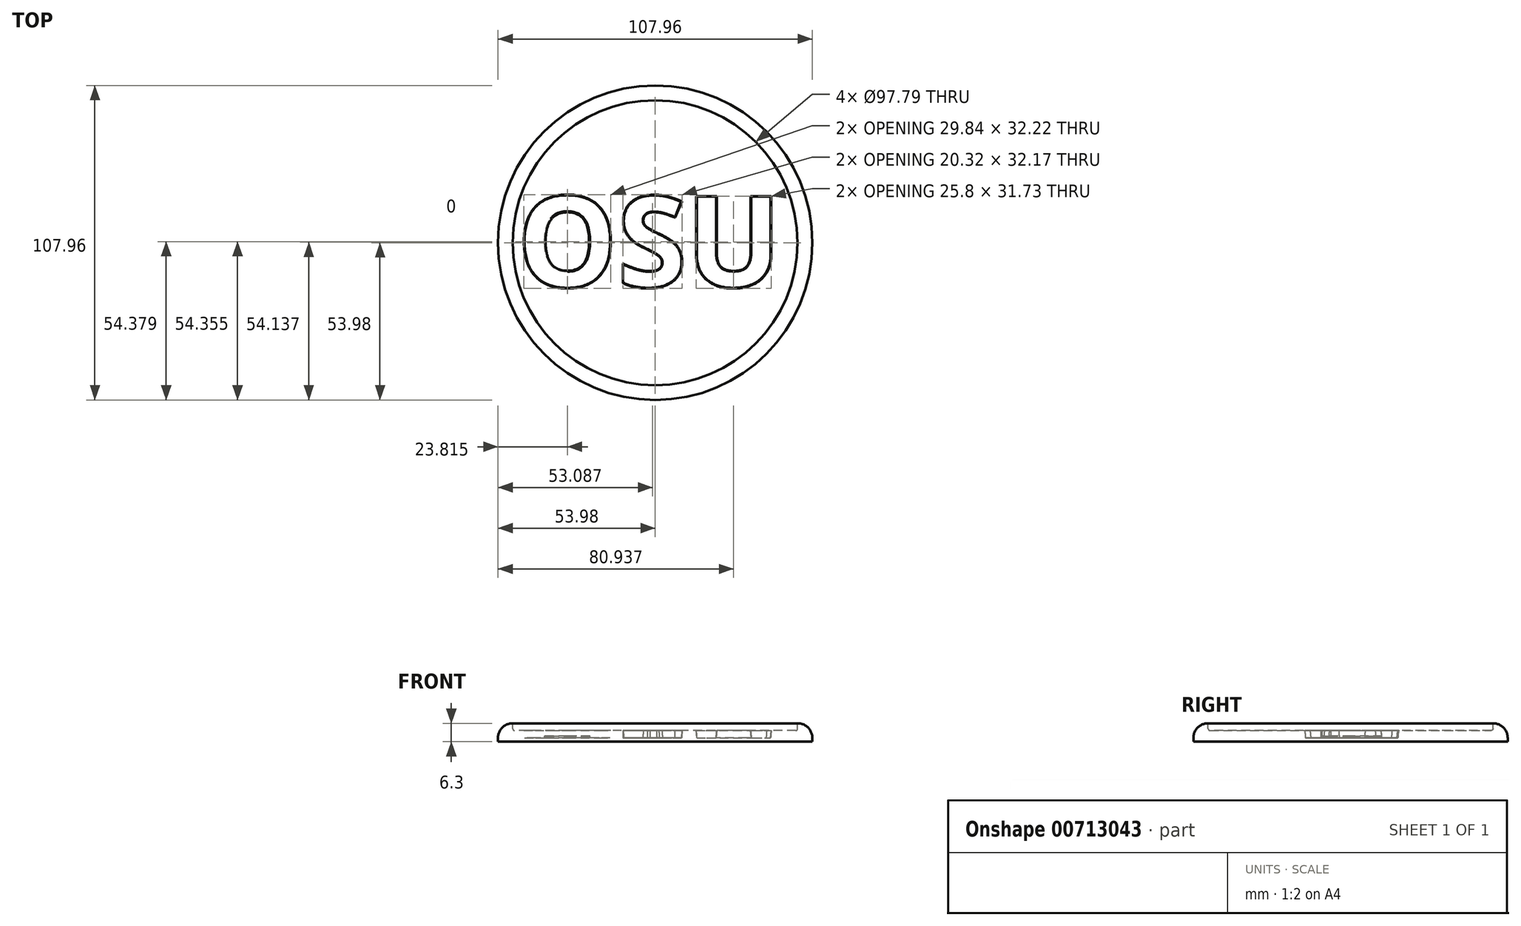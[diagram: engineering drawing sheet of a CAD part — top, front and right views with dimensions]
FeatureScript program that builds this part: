
annotation { "Feature Type Name" : "Feature", "Feature Type Description" : "" }
export const myFeature = defineFeature(function(context is Context, id is Id, definition is map)
    precondition{}
    {
        {
            var Q0;
            Q0=qCreatedBy(makeId("Top.planeOp"),FACE);
            var sketch = newSketch(context, id + "F0", { "sketchPlane" : qUnion([Q0])});
            skText(sketch, "E0", { "text": "OSU", "fontName": "OpenSans-Bold.ttf"});
            const initialGuessF0  = {"E0": [-0.0473, -0.015, 1, 0, 0.031]};
            skSetInitialGuess(sketch, initialGuessF0);
            skSolve(sketch);
        }
        {
            var Q0;
            Q0=qCreatedBy(makeId("Top.planeOp"),FACE);
            var sketch = newSketch(context, id + "F1", { "sketchPlane" : qUnion([Q0])});
            skCircle(sketch, "E1", {"center": v(0, 0) * mm, "radius": 53.98 * mm});
            skSolve(sketch);
        }
        {
            var Q0;
            Q0 = qSketchRegion(id + "F1", true);
            extrude(context, id + "F2", {"entities" : qUnion([Q0]), "oppositeDirection" : true, "depth" : 6.35 * mm, "offsetDistance" : 25.4 * mm});
        }
        {
            var Q0;
            Q0 = qSketchRegion(id + "F0", true);
            extrude(context, id + "F3", {"entities" : qUnion([Q0]), "operationType" : NewBodyOperationType.REMOVE, "oppositeDirection" : true, "depth" : 5.08 * mm, "offsetDistance" : 25.4 * mm});
        }
        {
            var Q0;
            Q0=makeQuery(id+"F2.opExtrude","CAP_EDGE",EDGE,{"disambiguationData":[OSD([sQuery(id+"F1.wireOp",EDGE,"E1")])],"isStart":true});
            fillet(context, id + "F4", {"entities" : qUnion([Q0]), "radius" : 5.08 * mm, "tangentPropagation" : true, "allowEdgeOverflow" : false});
        }
        {
            var Q0;
            Q0=makeQuery(id+"F3.boolean.opBoolean","COPY",EDGE,{"derivedFrom":makeQuery(id+"F3.opExtrude","CAP_EDGE",EDGE,{"disambiguationData":[OSD([sQuery(id+"F0.wireOp",EDGE,"E0.sketch_text.stroke-5")])],"isStart":true})});
            chamfer(context, id + "F5", {"entities" : qUnion([Q0]), "chamferType" : ChamferType.OFFSET_ANGLE, "width" : 0.5 * mm, "oppositeDirection" : false, "angle" : 85 * degree, "tangentPropagation" : true});
        }
        {
            var Q0;
            Q0=makeQuery(id+"F3.boolean.opBoolean","COPY",EDGE,{"derivedFrom":makeQuery(id+"F3.opExtrude","CAP_EDGE",EDGE,{"disambiguationData":[OSD([sQuery(id+"F0.wireOp",EDGE,"E0.sketch_text.stroke-26")])],"isStart":true})});
            var Q1;
            Q1=makeQuery(id+"F3.boolean.opBoolean","COPY",EDGE,{"derivedFrom":makeQuery(id+"F3.opExtrude","CAP_EDGE",EDGE,{"disambiguationData":[OSD([sQuery(id+"F0.wireOp",EDGE,"E0.sketch_text.stroke-23")])],"isStart":true})});
            var Q2;
            Q2=makeQuery(id+"F3.boolean.opBoolean","COPY",EDGE,{"derivedFrom":makeQuery(id+"F3.opExtrude","CAP_EDGE",EDGE,{"disambiguationData":[OSD([sQuery(id+"F0.wireOp",EDGE,"E0.sketch_text.stroke-22")])],"isStart":true})});
            var Q3;
            Q3=makeQuery(id+"F3.boolean.opBoolean","COPY",EDGE,{"derivedFrom":makeQuery(id+"F3.opExtrude","CAP_EDGE",EDGE,{"disambiguationData":[OSD([sQuery(id+"F0.wireOp",EDGE,"E0.sketch_text.stroke-14")])],"isStart":true})});
            var Q4;
            Q4=makeQuery(id+"F3.boolean.opBoolean","COPY",EDGE,{"derivedFrom":makeQuery(id+"F3.opExtrude","CAP_EDGE",EDGE,{"disambiguationData":[OSD([sQuery(id+"F0.wireOp",EDGE,"E0.sketch_text.stroke-40")])],"isStart":true})});
            var Q5;
            Q5=makeQuery(id+"F3.boolean.opBoolean","COPY",EDGE,{"derivedFrom":makeQuery(id+"F3.opExtrude","CAP_EDGE",EDGE,{"disambiguationData":[OSD([sQuery(id+"F0.wireOp",EDGE,"E0.sketch_text.stroke-37")])],"isStart":true})});
            var Q6;
            Q6=makeQuery(id+"F3.boolean.opBoolean","COPY",EDGE,{"derivedFrom":makeQuery(id+"F3.opExtrude","CAP_EDGE",EDGE,{"disambiguationData":[OSD([sQuery(id+"F0.wireOp",EDGE,"E0.sketch_text.stroke-16")])],"isStart":true})});
            var Q7;
            Q7=makeQuery(id+"F3.boolean.opBoolean","COPY",EDGE,{"derivedFrom":makeQuery(id+"F3.opExtrude","CAP_EDGE",EDGE,{"disambiguationData":[OSD([sQuery(id+"F0.wireOp",EDGE,"E0.sketch_text.stroke-15")])],"isStart":true})});
            var Q8;
            Q8=makeQuery(id+"F3.boolean.opBoolean","COPY",EDGE,{"derivedFrom":makeQuery(id+"F3.opExtrude","CAP_EDGE",EDGE,{"disambiguationData":[OSD([sQuery(id+"F0.wireOp",EDGE,"E0.sketch_text.stroke-41")])],"isStart":true})});
            var Q9;
            Q9=makeQuery(id+"F3.boolean.opBoolean","COPY",EDGE,{"derivedFrom":makeQuery(id+"F3.opExtrude","CAP_EDGE",EDGE,{"disambiguationData":[OSD([sQuery(id+"F0.wireOp",EDGE,"E0.sketch_text.stroke-39")])],"isStart":true})});
            var Q10;
            Q10=makeQuery(id+"F3.boolean.opBoolean","COPY",EDGE,{"derivedFrom":makeQuery(id+"F3.opExtrude","CAP_EDGE",EDGE,{"disambiguationData":[OSD([sQuery(id+"F0.wireOp",EDGE,"E0.sketch_text.stroke-38")])],"isStart":true})});
            var Q11;
            Q11=makeQuery(id+"F3.boolean.opBoolean","COPY",EDGE,{"derivedFrom":makeQuery(id+"F3.opExtrude","CAP_EDGE",EDGE,{"disambiguationData":[OSD([sQuery(id+"F0.wireOp",EDGE,"E0.sketch_text.stroke-36")])],"isStart":true})});
            var Q12;
            Q12=makeQuery(id+"F3.boolean.opBoolean","COPY",EDGE,{"derivedFrom":makeQuery(id+"F3.opExtrude","CAP_EDGE",EDGE,{"disambiguationData":[OSD([sQuery(id+"F0.wireOp",EDGE,"E0.sketch_text.stroke-35")])],"isStart":true})});
            var Q13;
            Q13=makeQuery(id+"F3.boolean.opBoolean","COPY",EDGE,{"derivedFrom":makeQuery(id+"F3.opExtrude","CAP_EDGE",EDGE,{"disambiguationData":[OSD([sQuery(id+"F0.wireOp",EDGE,"E0.sketch_text.stroke-34")])],"isStart":true})});
            var Q14;
            Q14=makeQuery(id+"F3.boolean.opBoolean","COPY",EDGE,{"derivedFrom":makeQuery(id+"F3.opExtrude","CAP_EDGE",EDGE,{"disambiguationData":[OSD([sQuery(id+"F0.wireOp",EDGE,"E0.sketch_text.stroke-33")])],"isStart":true})});
            var Q15;
            Q15=makeQuery(id+"F3.boolean.opBoolean","COPY",EDGE,{"derivedFrom":makeQuery(id+"F3.opExtrude","CAP_EDGE",EDGE,{"disambiguationData":[OSD([sQuery(id+"F0.wireOp",EDGE,"E0.sketch_text.stroke-32")])],"isStart":true})});
            var Q16;
            Q16=makeQuery(id+"F3.boolean.opBoolean","COPY",EDGE,{"derivedFrom":makeQuery(id+"F3.opExtrude","CAP_EDGE",EDGE,{"disambiguationData":[OSD([sQuery(id+"F0.wireOp",EDGE,"E0.sketch_text.stroke-18")])],"isStart":true})});
            var Q17;
            Q17=makeQuery(id+"F3.boolean.opBoolean","COPY",EDGE,{"derivedFrom":makeQuery(id+"F3.opExtrude","CAP_EDGE",EDGE,{"disambiguationData":[OSD([sQuery(id+"F0.wireOp",EDGE,"E0.sketch_text.stroke-19")])],"isStart":true})});
            var Q18;
            Q18=makeQuery(id+"F3.boolean.opBoolean","COPY",EDGE,{"derivedFrom":makeQuery(id+"F3.opExtrude","CAP_EDGE",EDGE,{"disambiguationData":[OSD([sQuery(id+"F0.wireOp",EDGE,"E0.sketch_text.stroke-20")])],"isStart":true})});
            var Q19;
            Q19=makeQuery(id+"F3.boolean.opBoolean","COPY",EDGE,{"derivedFrom":makeQuery(id+"F3.opExtrude","CAP_EDGE",EDGE,{"disambiguationData":[OSD([sQuery(id+"F0.wireOp",EDGE,"E0.sketch_text.stroke-21")])],"isStart":true})});
            var Q20;
            Q20=makeQuery(id+"F3.boolean.opBoolean","COPY",EDGE,{"derivedFrom":makeQuery(id+"F3.opExtrude","CAP_EDGE",EDGE,{"disambiguationData":[OSD([sQuery(id+"F0.wireOp",EDGE,"E0.sketch_text.stroke-25")])],"isStart":true})});
            var Q21;
            Q21=makeQuery(id+"F3.boolean.opBoolean","COPY",EDGE,{"derivedFrom":makeQuery(id+"F3.opExtrude","CAP_EDGE",EDGE,{"disambiguationData":[OSD([sQuery(id+"F0.wireOp",EDGE,"E0.sketch_text.stroke-24")])],"isStart":true})});
            var Q22;
            Q22=makeQuery(id+"F3.boolean.opBoolean","COPY",EDGE,{"derivedFrom":makeQuery(id+"F3.opExtrude","CAP_EDGE",EDGE,{"disambiguationData":[OSD([sQuery(id+"F0.wireOp",EDGE,"E0.sketch_text.stroke-27")])],"isStart":true})});
            var Q23;
            Q23=makeQuery(id+"F3.boolean.opBoolean","COPY",EDGE,{"derivedFrom":makeQuery(id+"F3.opExtrude","CAP_EDGE",EDGE,{"disambiguationData":[OSD([sQuery(id+"F0.wireOp",EDGE,"E0.sketch_text.stroke-28")])],"isStart":true})});
            var Q24;
            Q24=makeQuery(id+"F3.boolean.opBoolean","COPY",EDGE,{"derivedFrom":makeQuery(id+"F3.opExtrude","CAP_EDGE",EDGE,{"disambiguationData":[OSD([sQuery(id+"F0.wireOp",EDGE,"E0.sketch_text.stroke-29")])],"isStart":true})});
            var Q25;
            Q25=makeQuery(id+"F3.boolean.opBoolean","COPY",EDGE,{"derivedFrom":makeQuery(id+"F3.opExtrude","CAP_EDGE",EDGE,{"disambiguationData":[OSD([sQuery(id+"F0.wireOp",EDGE,"E0.sketch_text.stroke-30")])],"isStart":true})});
            var Q26;
            Q26=makeQuery(id+"F3.boolean.opBoolean","COPY",EDGE,{"derivedFrom":makeQuery(id+"F3.opExtrude","CAP_EDGE",EDGE,{"disambiguationData":[OSD([sQuery(id+"F0.wireOp",EDGE,"E0.sketch_text.stroke-31")])],"isStart":true})});
            chamfer(context, id + "F6", {"entities" : qUnion([Q0, Q1, Q2, Q3, Q4, Q5, Q6, Q7, Q8, Q9, Q10, Q11, Q12, Q13, Q14, Q15, Q16, Q17, Q18, Q19, Q20, Q21, Q22, Q23, Q24, Q25, Q26]), "chamferType" : ChamferType.OFFSET_ANGLE, "width" : 0.5 * mm, "oppositeDirection" : false, "angle" : 85 * degree, "tangentPropagation" : true});
        }
        {
            var Q0;
            Q0=makeQuery(id+"F3.boolean.opBoolean","COPY",EDGE,{"derivedFrom":makeQuery(id+"F3.opExtrude","CAP_EDGE",EDGE,{"disambiguationData":[OSD([sQuery(id+"F0.wireOp",EDGE,"E0.sketch_text.stroke-49")])],"isStart":true})});
            var Q1;
            Q1=makeQuery(id+"F3.boolean.opBoolean","COPY",EDGE,{"derivedFrom":makeQuery(id+"F3.opExtrude","CAP_EDGE",EDGE,{"disambiguationData":[OSD([sQuery(id+"F0.wireOp",EDGE,"E0.sketch_text.stroke-48")])],"isStart":true})});
            var Q2;
            Q2=makeQuery(id+"F3.boolean.opBoolean","COPY",EDGE,{"derivedFrom":makeQuery(id+"F3.opExtrude","CAP_EDGE",EDGE,{"disambiguationData":[OSD([sQuery(id+"F0.wireOp",EDGE,"E0.sketch_text.stroke-47")])],"isStart":true})});
            var Q3;
            Q3=makeQuery(id+"F3.boolean.opBoolean","COPY",EDGE,{"derivedFrom":makeQuery(id+"F3.opExtrude","CAP_EDGE",EDGE,{"disambiguationData":[OSD([sQuery(id+"F0.wireOp",EDGE,"E0.sketch_text.stroke-46")])],"isStart":true})});
            var Q4;
            Q4=makeQuery(id+"F3.boolean.opBoolean","COPY",EDGE,{"derivedFrom":makeQuery(id+"F3.opExtrude","CAP_EDGE",EDGE,{"disambiguationData":[OSD([sQuery(id+"F0.wireOp",EDGE,"E0.sketch_text.stroke-45")])],"isStart":true})});
            var Q5;
            Q5=makeQuery(id+"F3.boolean.opBoolean","COPY",EDGE,{"derivedFrom":makeQuery(id+"F3.opExtrude","CAP_EDGE",EDGE,{"disambiguationData":[OSD([sQuery(id+"F0.wireOp",EDGE,"E0.sketch_text.stroke-44")])],"isStart":true})});
            var Q6;
            Q6=makeQuery(id+"F3.boolean.opBoolean","COPY",EDGE,{"derivedFrom":makeQuery(id+"F3.opExtrude","CAP_EDGE",EDGE,{"disambiguationData":[OSD([sQuery(id+"F0.wireOp",EDGE,"E0.sketch_text.stroke-43")])],"isStart":true})});
            var Q7;
            Q7=makeQuery(id+"F3.boolean.opBoolean","COPY",EDGE,{"derivedFrom":makeQuery(id+"F3.opExtrude","CAP_EDGE",EDGE,{"disambiguationData":[OSD([sQuery(id+"F0.wireOp",EDGE,"E0.sketch_text.stroke-42")])],"isStart":true})});
            var Q8;
            Q8=makeQuery(id+"F3.boolean.opBoolean","COPY",EDGE,{"derivedFrom":makeQuery(id+"F3.opExtrude","CAP_EDGE",EDGE,{"disambiguationData":[OSD([sQuery(id+"F0.wireOp",EDGE,"E0.sketch_text.stroke-56")])],"isStart":true})});
            var Q9;
            Q9=makeQuery(id+"F3.boolean.opBoolean","COPY",EDGE,{"derivedFrom":makeQuery(id+"F3.opExtrude","CAP_EDGE",EDGE,{"disambiguationData":[OSD([sQuery(id+"F0.wireOp",EDGE,"E0.sketch_text.stroke-55")])],"isStart":true})});
            var Q10;
            Q10=makeQuery(id+"F3.boolean.opBoolean","COPY",EDGE,{"derivedFrom":makeQuery(id+"F3.opExtrude","CAP_EDGE",EDGE,{"disambiguationData":[OSD([sQuery(id+"F0.wireOp",EDGE,"E0.sketch_text.stroke-54")])],"isStart":true})});
            var Q11;
            Q11=makeQuery(id+"F3.boolean.opBoolean","COPY",EDGE,{"derivedFrom":makeQuery(id+"F3.opExtrude","CAP_EDGE",EDGE,{"disambiguationData":[OSD([sQuery(id+"F0.wireOp",EDGE,"E0.sketch_text.stroke-53")])],"isStart":true})});
            var Q12;
            Q12=makeQuery(id+"F3.boolean.opBoolean","COPY",EDGE,{"derivedFrom":makeQuery(id+"F3.opExtrude","CAP_EDGE",EDGE,{"disambiguationData":[OSD([sQuery(id+"F0.wireOp",EDGE,"E0.sketch_text.stroke-52")])],"isStart":true})});
            var Q13;
            Q13=makeQuery(id+"F3.boolean.opBoolean","COPY",EDGE,{"derivedFrom":makeQuery(id+"F3.opExtrude","CAP_EDGE",EDGE,{"disambiguationData":[OSD([sQuery(id+"F0.wireOp",EDGE,"E0.sketch_text.stroke-51")])],"isStart":true})});
            var Q14;
            Q14=makeQuery(id+"F3.boolean.opBoolean","COPY",EDGE,{"derivedFrom":makeQuery(id+"F3.opExtrude","CAP_EDGE",EDGE,{"disambiguationData":[OSD([sQuery(id+"F0.wireOp",EDGE,"E0.sketch_text.stroke-50")])],"isStart":true})});
            chamfer(context, id + "F7", {"entities" : qUnion([Q0, Q1, Q2, Q3, Q4, Q5, Q6, Q7, Q8, Q9, Q10, Q11, Q12, Q13, Q14]), "chamferType" : ChamferType.OFFSET_ANGLE, "width" : 0.5 * mm, "oppositeDirection" : false, "angle" : 85 * degree, "tangentPropagation" : true});
        }
        {
            var Q0;
            {var subQ0=sQuery(id+"F1.wireOp",EDGE,"E1");Q0=makeQuery(id+"F3.boolean.opBoolean","SPLIT",FACE,{"disambiguationData":[TD([makeQuery(id+"F2.opExtrude","SWEPT_FACE",FACE,{"disambiguationData":[OSD([subQ0])]})])],"derivedFrom":makeQuery(id+"F2.opExtrude","CAP_FACE",FACE,{"disambiguationData":[OSD([subQ0])],"isStart":true})});}
            var sketch = newSketch(context, id + "F8", { "sketchPlane" : qUnion([Q0])});
            skCircle(sketch, "E2", {"center": v(0, 0) * mm, "radius": 48.9 * mm});
            skSolve(sketch);
        }
        {
            var Q0;
            Q0 = qSketchRegion(id + "F8", true);
            extrude(context, id + "F9", {"entities" : qUnion([Q0]), "operationType" : NewBodyOperationType.REMOVE, "oppositeDirection" : true, "depth" : 2.54 * mm, "offsetDistance" : 25.4 * mm});
        }
        {
            var Q0;
            {var subQ0=sQuery(id+"F1.wireOp",EDGE,"E1");Q0=makeQuery(id+"F9.boolean.opBoolean","MERGE",EDGE,{"derivedFrom":[makeQuery(id+"F4.opFillet","BLEND_EDGE",EDGE,{"blendedFrom":[makeQuery(id+"F2.opExtrude","CAP_EDGE",EDGE,{"disambiguationData":[OSD([subQ0])],"isStart":true}),makeQuery(id+"F3.boolean.opBoolean","SPLIT",FACE,{"disambiguationData":[TD([makeQuery(id+"F2.opExtrude","SWEPT_FACE",FACE,{"disambiguationData":[OSD([subQ0])]})])],"derivedFrom":makeQuery(id+"F2.opExtrude","CAP_FACE",FACE,{"disambiguationData":[OSD([subQ0])],"isStart":true})})],"blendedInto":[makeQuery(id+"F3.boolean.opBoolean","SPLIT",FACE,{"disambiguationData":[TD([makeQuery(id+"F2.opExtrude","SWEPT_FACE",FACE,{"disambiguationData":[OSD([subQ0])]})])],"derivedFrom":makeQuery(id+"F2.opExtrude","CAP_FACE",FACE,{"disambiguationData":[OSD([subQ0])],"isStart":true})})]}),makeQuery(id+"F9.opExtrude","CAP_EDGE",EDGE,{"disambiguationData":[OSD([sQuery(id+"F8.wireOp",EDGE,"E2")])],"isStart":true})]});}
            var Q1;
            Q1=makeQuery(id+"F9.boolean.opBoolean","COPY",EDGE,{"derivedFrom":makeQuery(id+"F9.opExtrude","CAP_EDGE",EDGE,{"disambiguationData":[OSD([sQuery(id+"F8.wireOp",EDGE,"E2")])],"isStart":false})});
            fillet(context, id + "F10", {"entities" : qUnion([Q0, Q1]), "radius" : 0.64 * mm, "tangentPropagation" : true, "allowEdgeOverflow" : false});
        }
        {
            var Q0;
            Q0=makeQuery(id+"F9.boolean.opBoolean","INTERSECT",EDGE,{"derivedFrom":[makeQuery(id+"F3.boolean.opBoolean","COPY",FACE,{"derivedFrom":makeQuery(id+"F3.opExtrude","SWEPT_FACE",FACE,{"disambiguationData":[OSD([sQuery(id+"F0.wireOp",EDGE,"E0.sketch_text.stroke-10")])]})}),makeQuery(id+"F9.opExtrude","CAP_FACE",FACE,{"disambiguationData":[OSD([sQuery(id+"F8.wireOp",EDGE,"E2")])],"isStart":false})]});
            chamfer(context, id + "F11", {"entities" : qUnion([Q0]), "chamferType" : ChamferType.OFFSET_ANGLE, "width" : 1.9 * mm, "oppositeDirection" : false, "angle" : 10 * degree, "tangentPropagation" : true});
        }
    });
